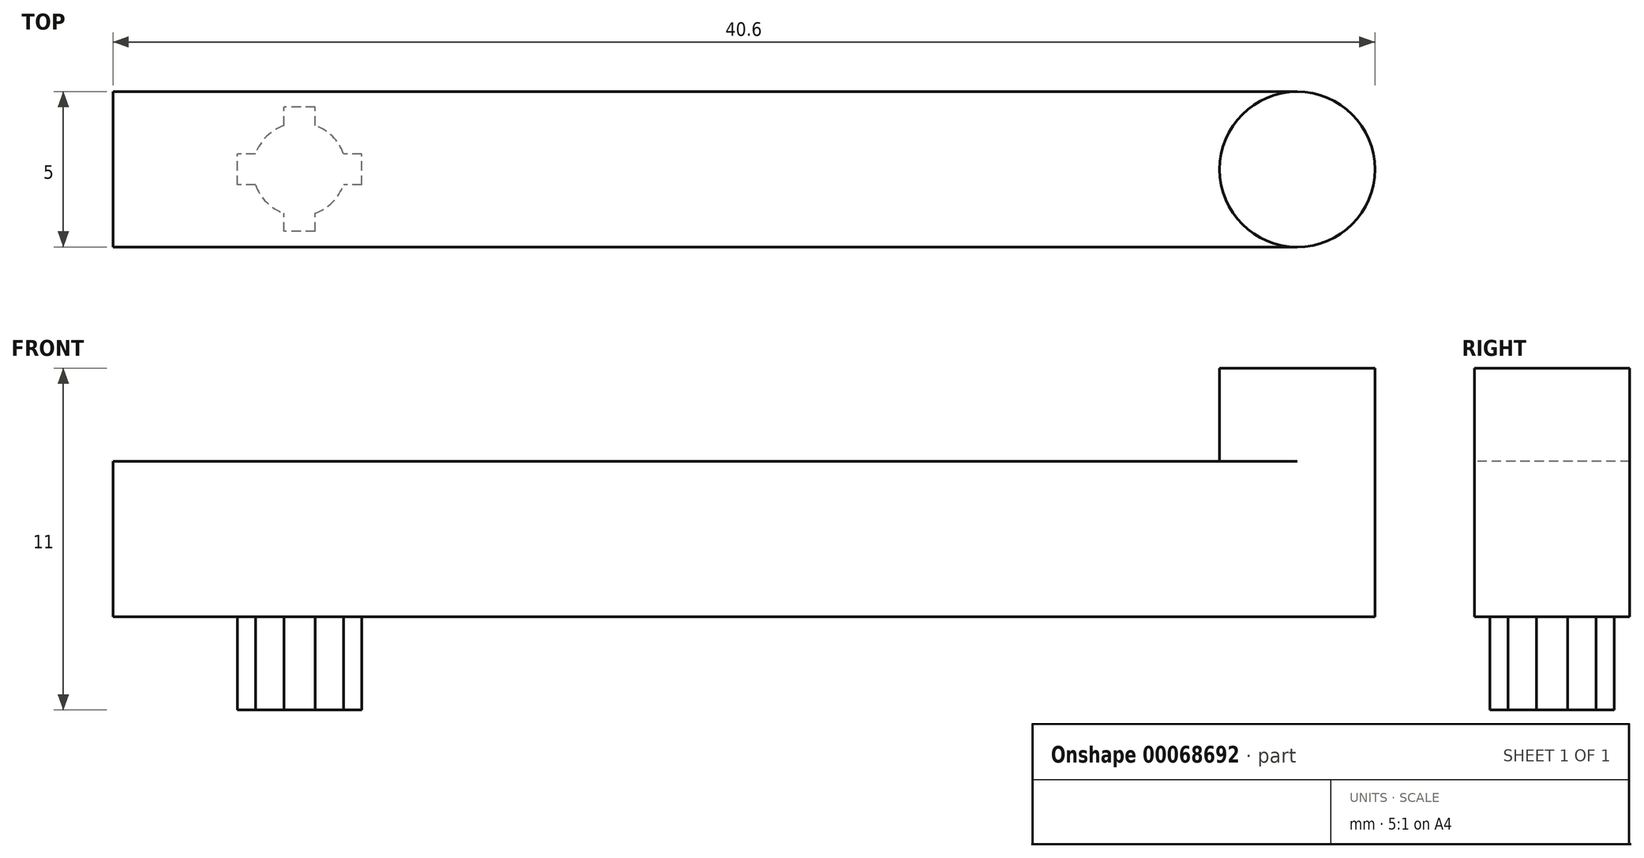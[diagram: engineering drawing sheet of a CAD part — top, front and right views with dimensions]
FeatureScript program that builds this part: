
annotation { "Feature Type Name" : "Feature", "Feature Type Description" : "" }
export const myFeature = defineFeature(function(context is Context, id is Id, definition is map)
    precondition{}
    {
        {
            var Q0;
            Q0=qCreatedBy(makeId("Top.planeOp"),FACE);
            var sketch = newSketch(context, id + "F0", { "sketchPlane" : qUnion([Q0])});
            skCircle(sketch, "E0", {"center": v(0, 0) * mm, "radius": 2.5 * mm});
            skSolve(sketch);
        }
        {
            var Q0;
            Q0 = qSketchRegion(id + "F0", true);
            extrude(context, id + "F1", {"entities" : qUnion([Q0]), "oppositeDirection" : true, "depth" : 3 * mm});
        }
        {
            var Q0;
            Q0=makeQuery(id+"F1.opExtrude","CAP_FACE",FACE,{"disambiguationData":[OSD([sQuery(id+"F0.wireOp",EDGE,"E0")])],"isStart":false});
            var sketch = newSketch(context, id + "F2", { "sketchPlane" : qUnion([Q0])});
            skArc(sketch, "E1", {"start": v(0, -2.5) * mm, "mid": v(2.5, 0) * mm, "end": v(0, 2.5) * mm});
            skLineSegment(sketch, "E2", {"start": v(0, 2.5) * mm, "end": v(-38.1, 2.5) * mm});
            skLineSegment(sketch, "E3", {"start": v(0, -2.5) * mm, "end": v(-38.1, -2.5) * mm});
            skLineSegment(sketch, "E4", {"start": v(-38.1, -2.5) * mm, "end": v(-38.1, 2.5) * mm});
            skSolve(sketch);
        }
        {
            var Q0;
            Q0 = qSketchRegion(id + "F2", true);
            extrude(context, id + "F3", {"entities" : qUnion([Q0]), "operationType" : NewBodyOperationType.ADD, "depth" : 5 * mm});
        }
        {
            var Q0;
            Q0=makeQuery(id+"F3.opExtrude","CAP_FACE",FACE,{"disambiguationData":[OSD([sQuery(id+"F2.wireOp",EDGE,"E1"),sQuery(id+"F2.wireOp",EDGE,"E2"),sQuery(id+"F2.wireOp",EDGE,"E3"),sQuery(id+"F2.wireOp",EDGE,"E4")])],"isStart":false});
            var sketch = newSketch(context, id + "F4", { "sketchPlane" : qUnion([Q0])});
            skArc(sketch, "E5", {"start": v(-32.6, 1.41) * mm, "mid": v(-33.16, 1.06) * mm, "end": v(-33.51, 0.5) * mm});
            skLineSegment(sketch, "E6.rect.bottom", {"start": v(-30.1, 0.5) * mm, "end": v(-30.69, 0.5) * mm});
            skLineSegment(sketch, "E6.rect.top", {"start": v(-30.1, -0.5) * mm, "end": v(-30.69, -0.5) * mm});
            skLineSegment(sketch, "E6.rect.left", {"start": v(-30.1, 0.5) * mm, "end": v(-30.1, -0.5) * mm});
            skLineSegment(sketch, "E6.rect.right", {"start": v(-34.1, 0.5) * mm, "end": v(-34.1, -0.5) * mm});
            skLineSegment(sketch, "E7.rect.bottom", {"start": v(-31.6, 2) * mm, "end": v(-32.6, 2) * mm});
            skLineSegment(sketch, "E7.rect.top", {"start": v(-31.6, -2) * mm, "end": v(-32.6, -2) * mm});
            skLineSegment(sketch, "E7.rect.left", {"start": v(-31.6, 2) * mm, "end": v(-31.6, 1.41) * mm});
            skLineSegment(sketch, "E7.rect.right", {"start": v(-32.6, 2) * mm, "end": v(-32.6, 1.41) * mm});
            skLineSegment(sketch, "E8.trimOffspring", {"start": v(-33.51, 0.5) * mm, "end": v(-34.1, 0.5) * mm});
            skLineSegment(sketch, "E9.trimOffspring", {"start": v(-32.6, -1.41) * mm, "end": v(-32.6, -2) * mm});
            skLineSegment(sketch, "E10.trimOffspring", {"start": v(-31.6, -1.41) * mm, "end": v(-31.6, -2) * mm});
            skLineSegment(sketch, "E11.trimOffspring", {"start": v(-33.51, -0.5) * mm, "end": v(-34.1, -0.5) * mm});
            skArc(sketch, "E12.trimOffspring", {"start": v(-33.51, -0.5) * mm, "mid": v(-33.16, -1.06) * mm, "end": v(-32.6, -1.41) * mm});
            skArc(sketch, "E13.trimOffspring", {"start": v(-31.6, -1.41) * mm, "mid": v(-31.04, -1.06) * mm, "end": v(-30.69, -0.5) * mm});
            skArc(sketch, "E14.trimOffspring", {"start": v(-30.69, 0.5) * mm, "mid": v(-31.04, 1.06) * mm, "end": v(-31.6, 1.41) * mm});
            skSolve(sketch);
        }
        {
            var Q0;
            Q0 = qSketchRegion(id + "F4", true);
            extrude(context, id + "F5", {"entities" : qUnion([Q0]), "operationType" : NewBodyOperationType.ADD, "depth" : 3 * mm});
        }
    });
